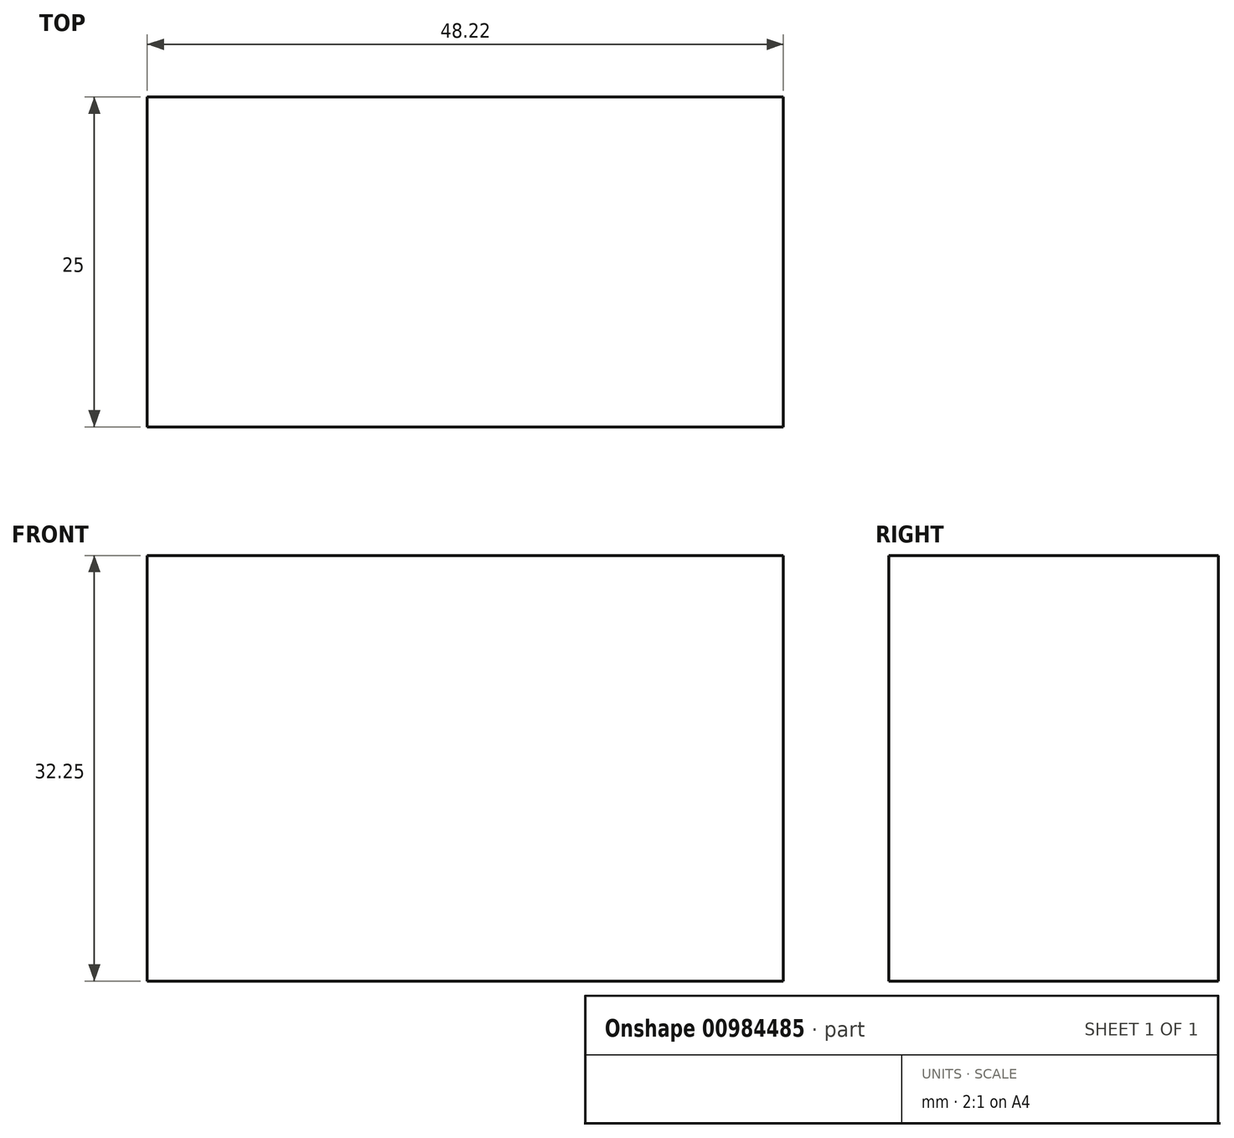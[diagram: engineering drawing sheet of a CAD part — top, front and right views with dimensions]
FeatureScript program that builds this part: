
annotation { "Feature Type Name" : "Feature", "Feature Type Description" : "" }
export const myFeature = defineFeature(function(context is Context, id is Id, definition is map)
    precondition{}
    {
        {
            var Q0;
            Q0=qCreatedBy(makeId("Front.planeOp"),FACE);
            var sketch = newSketch(context, id + "F0", { "sketchPlane" : qUnion([Q0])});
            skLineSegment(sketch, "E0.bottom", {"start": v(-100.97, 57.2) * mm, "end": v(-52.75, 57.2) * mm});
            skLineSegment(sketch, "E0.top", {"start": v(-100.97, 24.96) * mm, "end": v(-52.75, 24.96) * mm});
            skLineSegment(sketch, "E0.left", {"start": v(-100.97, 57.2) * mm, "end": v(-100.97, 24.96) * mm});
            skLineSegment(sketch, "E0.right", {"start": v(-52.75, 57.2) * mm, "end": v(-52.75, 24.96) * mm});
            skSolve(sketch);
        }
        {
            var Q0;
            Q0 = qSketchRegion(id + "F0", true);
            extrude(context, id + "F1", {"entities" : qUnion([Q0]), "depth" : 25 * mm, "offsetDistance" : 25 * mm});
        }
    });
